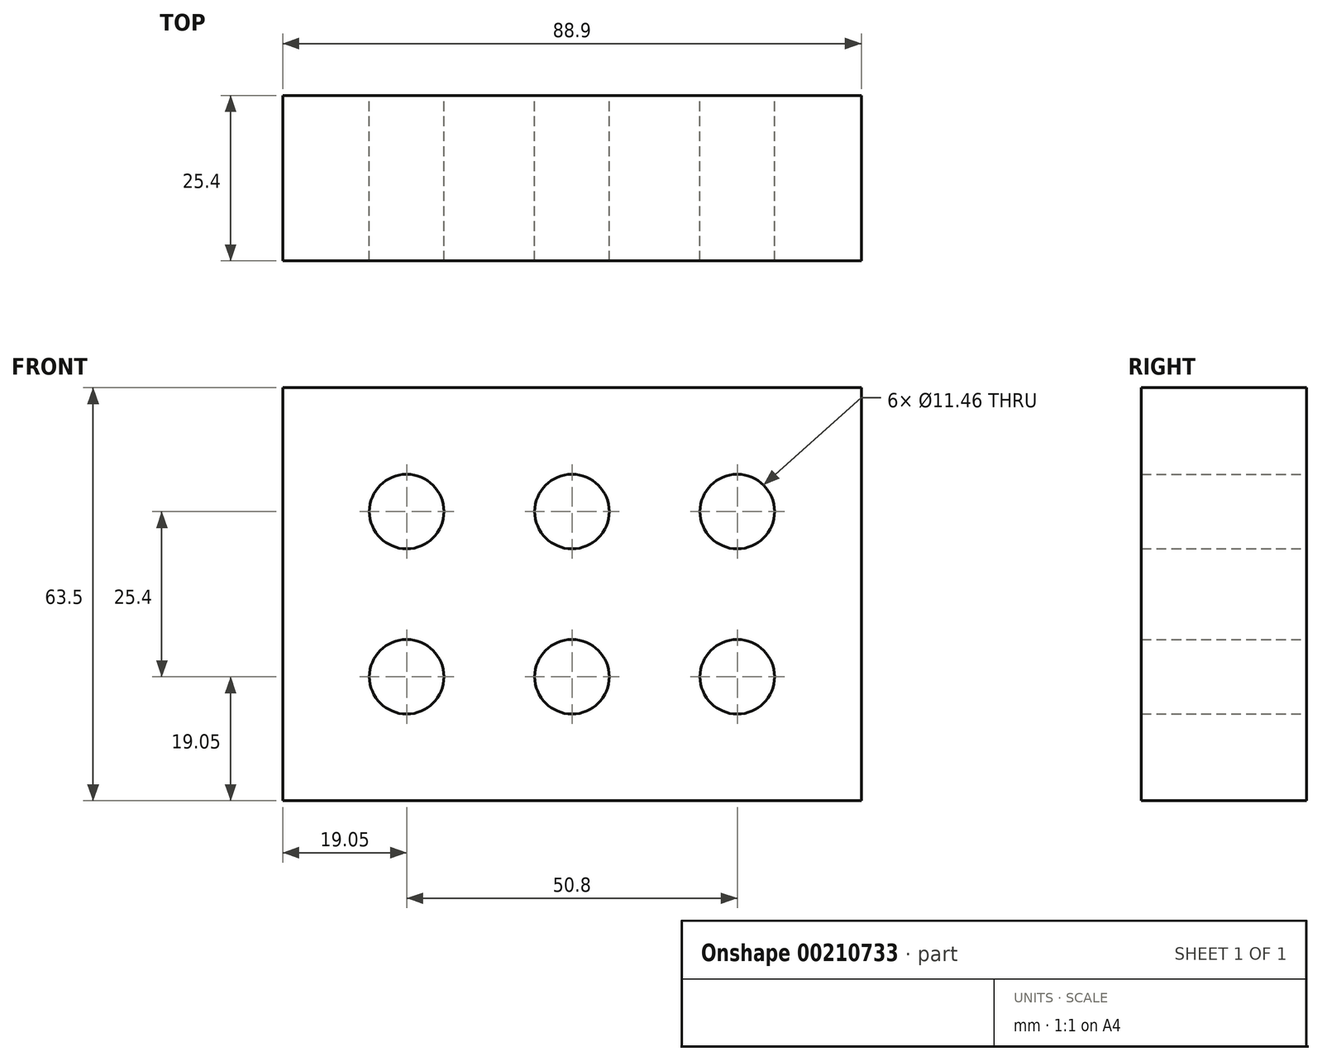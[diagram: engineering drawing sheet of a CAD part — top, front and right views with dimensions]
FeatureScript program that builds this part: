
annotation { "Feature Type Name" : "Feature", "Feature Type Description" : "" }
export const myFeature = defineFeature(function(context is Context, id is Id, definition is map)
    precondition{}
    {
        {
            var Q0;
            Q0=qCreatedBy(makeId("Front.planeOp"),FACE);
            var sketch = newSketch(context, id + "F0", { "sketchPlane" : qUnion([Q0])});
            skLineSegment(sketch, "E0.bottom", {"start": v(-44.45, 31.75) * mm, "end": v(44.45, 31.75) * mm});
            skLineSegment(sketch, "E0.top", {"start": v(-44.45, -31.75) * mm, "end": v(44.45, -31.75) * mm});
            skLineSegment(sketch, "E0.left", {"start": v(-44.45, 31.75) * mm, "end": v(-44.45, -31.75) * mm});
            skLineSegment(sketch, "E0.right", {"start": v(44.45, 31.75) * mm, "end": v(44.45, -31.75) * mm});
            skCircle(sketch, "E1", {"center": v(-25.4, 12.7) * mm, "radius": 5.73 * mm});
            skCircle(sketch, "E2", {"center": v(0, 12.7) * mm, "radius": 5.73 * mm});
            skCircle(sketch, "E3", {"center": v(25.4, 12.7) * mm, "radius": 5.73 * mm});
            skCircle(sketch, "E4", {"center": v(-25.4, -12.7) * mm, "radius": 5.73 * mm});
            skCircle(sketch, "E5", {"center": v(0, -12.7) * mm, "radius": 5.73 * mm});
            skCircle(sketch, "E6", {"center": v(25.4, -12.7) * mm, "radius": 5.73 * mm});
            skLineSegment(sketch, "E7", {"start": v(-25.4, 12.7) * mm, "end": v(25.4, 12.7) * mm});
            skLineSegment(sketch, "E8", {"start": v(-25.4, -12.7) * mm, "end": v(-25.4, 12.7) * mm});
            skLineSegment(sketch, "E9", {"start": v(25.4, 12.7) * mm, "end": v(25.4, -12.7) * mm});
            skLineSegment(sketch, "E10", {"start": v(-25.4, -12.7) * mm, "end": v(25.4, -12.7) * mm});
            skSolve(sketch);
        }
        {
            var Q0;
            Q0=makeQuery(id+"F0.imprint","IMPRINT",FACE,{"disambiguationData":[TD([[makeQuery(id+"F0.imprint","IMPRINT",EDGE,{"derivedFrom":sQuery(id+"F0.wireOp",EDGE,"E0.bottom")}),-1.0]])]});
            var Q1;
            {var subQ1=sQuery(id+"F0.wireOp",EDGE,"E1");var subQ5=sQuery(id+"F0.wireOp",EDGE,"E7");var subQ16=makeQuery(id+"F0.imprint","INTERSECT",VERTEX,{"derivedFrom":[subQ1,subQ5]});Q1=makeQuery(id+"F0.imprint","IMPRINT",FACE,{"disambiguationData":[TD([[makeQuery(id+"F0.imprint","IMPRINT",EDGE,{"disambiguationData":[TD([[subQ16,1.0]])],"derivedFrom":subQ1}),-1.0]])]});}
            extrude(context, id + "F1", {"entities" : qUnion([Q0, Q1]), "depth" : 25.4 * mm});
        }
    });
